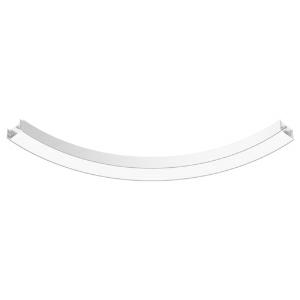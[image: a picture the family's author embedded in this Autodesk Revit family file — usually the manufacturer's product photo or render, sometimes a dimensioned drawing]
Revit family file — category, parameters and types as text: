
# Revit family: super-g_super-g__3100___90deg_hl_led__36_8w_5680lm_3000k_cri_80_430-1060_8a96
name_source: partatom
category: Leuchten
revit_build: Autodesk Revit 2016 (Build: 20190508_0715(x64)
units: mm (PartAtom-declared; Revit-internal decimal feet)

## family parameters
Basisbauteil = Fläche
Beim Laden mit Abzugskörper schneiden = Nein
Bemaßung runder Anschluss = Durchmesser verwenden
Gemeinsam genutzt = Nein
Lichtquelle = Nein
Raumberechnungspunkt = Nein
Teiletyp = Normal

## types (1)
- 430-1060- (1 x LED, 710 lm, 3000K)
    Approval mark = CE
    Beschreibung = The insert consists of aluminum-extruded profile. Charming SOFT-EDGE design ensure unparalleled styling. The ballast is integrated and allows for an operation with 220-240V (50/60Hz). SUPER-G (# 430-1060) ist not dimmable (on/off).
    CIE Flux Codes = 44 75 94 100 65
    Color Rendering = 1B/80…89
    Color Temperature = 3000K
    Height = 120 mm
    Hersteller = Prolicht
    Lamp Light Flux = 710 lm
    Lamp count = 1
    Lampe = 1 x LED
    Length = 304 mm
    Luminous efficacy = 90 lm/W
    ModVariant = Nein
    Modell = 430-1060
    Mounting Place = Ceiling
    Mounting Type = Pendant
    Number of Poles = 1
    OnlyDefault = Ja
    Power Factor = 1
    Product Name = SUPER-G__SUPER-G  3100 / 90° HL LED: 36,8W 5680lm 3000K CRI:80
    Product group = Suspended profile systems
    ProductGroupID = 944
    Protection Class = Protection class I
    Protection Degree = IP 20
    RLX_Detail_Level = 1
    RlxData = <blob elided: 26413 chars, md5=a36ec14d>
    Scheinlast = 41 VA
    Socket = socket
    Standby Power = 0 W
    System Light Flux = 3692 lm
    System Power = 41 W
    Typenbild = 430-1060.jpg
    URL = http://relux.com
    VarID = 430-1060-
    Voltage = 0 V
    Vorgabe-Ansicht = 1800 mm
    Weight = 0.00 kg
    Width = 150 mm

## geometry (parser evidence)
native form markers: Blend x4, Sweep x28
no freeform markers — native parametric forms only
